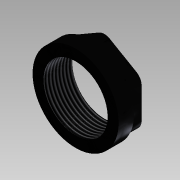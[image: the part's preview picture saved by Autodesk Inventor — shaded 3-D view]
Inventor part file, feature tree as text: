
AUTODESK INVENTOR PART (.ipt)
format: ipt  version: 2015 SP1 (Build 190203100, 203)  size: 117,760 bytes
history: native  units: mm
features: extrude x2, sketch x2, thread x1, fillet x1
ambient origin geometry x8: Origin, YZ Plane, XZ Plane, XY Plane, X Axis, Y Axis, Z Axis, Center Point
bodies: Solid1 (feature_tree)
feature tree (6):
  extrude  "Extrusion1"  Depth=4.45mm
  thread  "Thread1"  [1 undecoded]
  extrude  "Extrusion2"  Depth=3.81mm TaperAngle=0.0deg
  fillet  "Fillet1"  Radius=3.0mm
  sketch  "Sketch1"  dims[d0=18.4mm d1=3.15mm d2=4.45mm d3=0.0mm]
  sketch  "Sketch2"  dims[d4=10.0mm d5=0.0mm d6=3.81mm d7=0.0mm d8=3.0mm d9=24.7mm]
note: 1 required parameter value undecoded (feature->parameter linkage not recoverable at this tier; creation-order binding heuristic only, values carry confidence <= 0.55)
